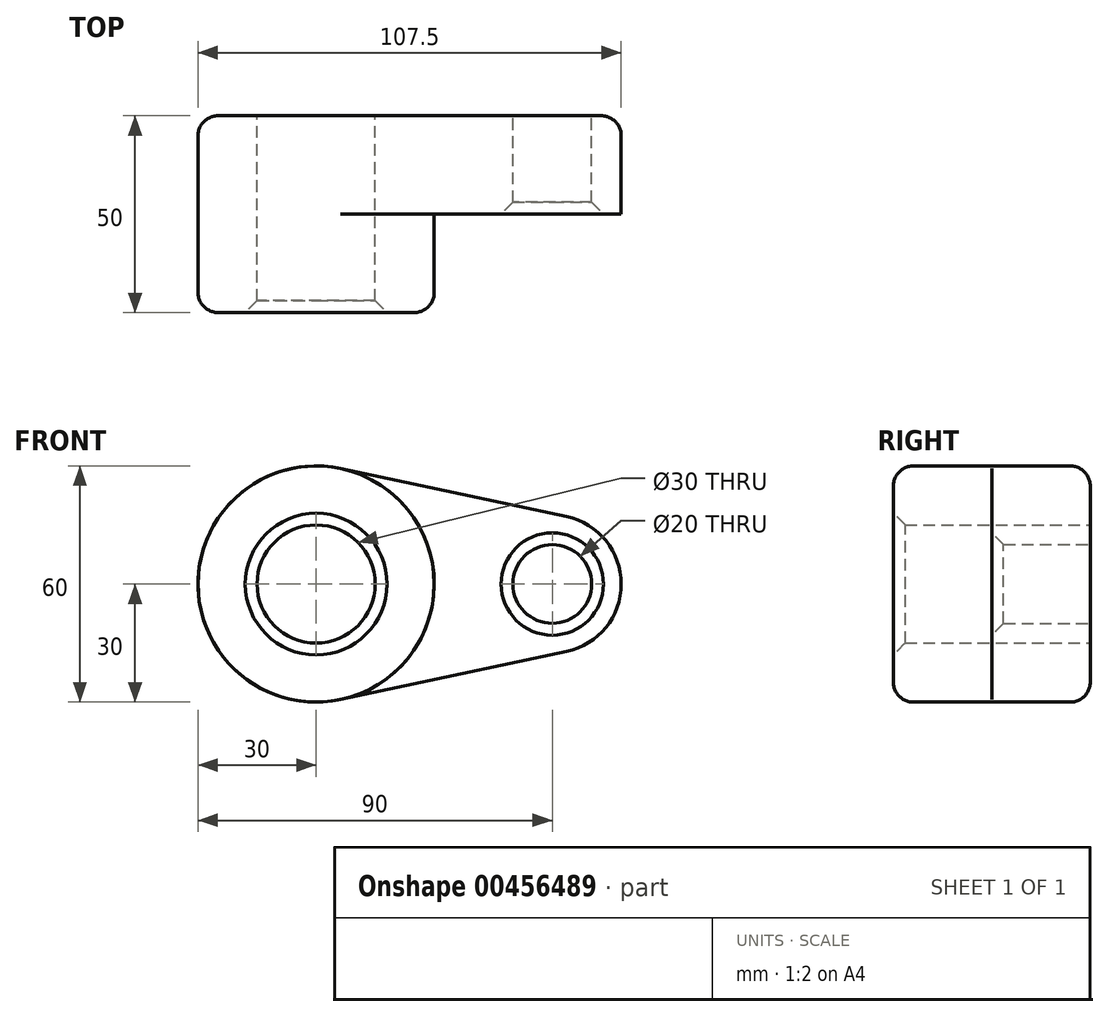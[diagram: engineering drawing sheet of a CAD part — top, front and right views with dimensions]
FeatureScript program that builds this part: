
annotation { "Feature Type Name" : "Feature", "Feature Type Description" : "" }
export const myFeature = defineFeature(function(context is Context, id is Id, definition is map)
    precondition{}
    {
        {
            var Q0;
            Q0=qCreatedBy(makeId("Front.planeOp"),FACE);
            var sketch = newSketch(context, id + "F0", { "sketchPlane" : qUnion([Q0])});
            skCircle(sketch, "E0", {"center": v(0, 0) * mm, "radius": 30 * mm});
            skCircle(sketch, "E1", {"center": v(60, 0) * mm, "radius": 17.5 * mm});
            skLineSegment(sketch, "E2", {"start": v(6.25, 29.34) * mm, "end": v(63.65, 17.12) * mm});
            skLineSegment(sketch, "E3", {"start": v(6.25, -29.34) * mm, "end": v(63.65, -17.12) * mm});
            skCircle(sketch, "E4", {"center": v(0, 0) * mm, "radius": 15 * mm});
            skCircle(sketch, "E5", {"center": v(60, 0) * mm, "radius": 10 * mm});
            skSolve(sketch);
        }
        {
            var Q0;
            Q0 = qSketchRegion(id + "F0", true);
            extrude(context, id + "F1", {"entities" : qUnion([Q0]), "depth" : 25 * mm, "offsetDistance" : 25.4 * mm});
        }
        {
            var Q0;
            Q0=makeQuery(id+"F0.imprint","IMPRINT",FACE,{"disambiguationData":[TD([[makeQuery(id+"F0.imprint","IMPRINT",EDGE,{"derivedFrom":sQuery(id+"F0.wireOp",EDGE,"E4")}),-1.0]])]});
            extrude(context, id + "F2", {"entities" : qUnion([Q0]), "operationType" : NewBodyOperationType.ADD, "depth" : 50 * mm, "offsetDistance" : 25.4 * mm});
        }
        {
            var Q0;
            Q0=makeQuery(id+"F1.opExtrude","CAP_EDGE",EDGE,{"disambiguationData":[OSD([sQuery(id+"F0.wireOp",EDGE,"E3")])],"isStart":true});
            var Q1;
            Q1=makeQuery(id+"F2.opExtrude","CAP_EDGE",EDGE,{"disambiguationData":[OSD([sQuery(id+"F0.wireOp",EDGE,"E0")])],"isStart":false});
            fillet(context, id + "F3", {"entities" : qUnion([Q0, Q1]), "radius" : 5.08 * mm, "tangentPropagation" : true, "allowEdgeOverflow" : false});
        }
        {
            var Q0;
            Q0=makeQuery(id+"F2.opExtrude","CAP_EDGE",EDGE,{"disambiguationData":[OSD([sQuery(id+"F0.wireOp",EDGE,"E4")])],"isStart":false});
            var Q1;
            {var subQ0=sQuery(id+"F0.wireOp",EDGE,"E0");Q1=makeQuery(id+"F3.opFillet","BLEND_EDGE",EDGE,{"blendedFrom":[makeQuery(id+"F2.opExtrude","CAP_EDGE",EDGE,{"disambiguationData":[OSD([subQ0])],"isStart":false}),makeQuery(id+"F2.opExtrude","CAP_FACE",FACE,{"disambiguationData":[OSD([subQ0,sQuery(id+"F0.wireOp",EDGE,"E4")])],"isStart":false})],"blendedInto":[makeQuery(id+"F2.opExtrude","CAP_FACE",FACE,{"disambiguationData":[OSD([subQ0,sQuery(id+"F0.wireOp",EDGE,"E4")])],"isStart":false})]});}
            var Q2;
            Q2=makeQuery(id+"F1.opExtrude","CAP_EDGE",EDGE,{"disambiguationData":[OSD([sQuery(id+"F0.wireOp",EDGE,"E5")])],"isStart":false});
            chamfer(context, id + "F4", {"entities" : qUnion([Q0, Q1, Q2]), "width" : 3 * mm, "tangentPropagation" : true});
        }
    });
